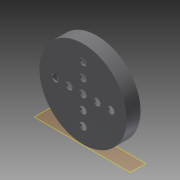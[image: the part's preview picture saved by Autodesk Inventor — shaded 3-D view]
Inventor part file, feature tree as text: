
AUTODESK INVENTOR PART (.ipt)
format: ipt  version: 2015 (Build 190159000, 159)  size: 233,472 bytes
history: native  units: mm
features: extrude x7, sketch x7, projected_geometry x2, plane x1
ambient origin geometry x8: Origin, YZ Plane, XZ Plane, XY Plane, X Axis, Y Axis, Z Axis, Center Point
bodies: Solid1 (feature_tree)
feature tree (17):
  extrude  "Extrusion1"  Depth=20.0mm TaperAngle=0.0deg
  extrude  "Extrusion2"  Depth=2.5mm TaperAngle=0.0deg
  extrude  "Extrusion3"  Depth=15.0mm
  extrude  "Extrusion4"  Depth=10.0mm
  plane  "Work Plane1"
  extrude  "Extrusion5"  Depth=10.0mm
  extrude  "Extrusion6"  Depth=10.0mm
  extrude  "Extrusion7"  Depth=10.0mm
  sketch  "Sketch1"  dims[d0=125.0mm d1=20.0mm d2=0.0mm]
  sketch  "Sketch2"  dims[d3=120.0mm d4=2.5mm d5=0.0mm]
  sketch  "Sketch3"  dims[d6=115.0mm d7=15.0mm]
  sketch  "Sketch4"  dims[d8=0.0mm d9=10.0mm]
  sketch  "Sketch5"  dims[d10=10.0mm d11=10.0mm]
  projected_geometry  "Projected Loop1"
  sketch  "Sketch6"  dims[d12=10.0mm d13=10.0mm]
  sketch  "Sketch7"  dims[d14=10.0mm d15=10.0mm d16=10.0mm d17=10.0mm d18=20.0mm d19=20.0mm d20=20.0mm d21=20.0mm d22=20.0mm d23=20.0mm d24=20.0mm d25=20.0mm d26=17.5mm d27=0.0mm d28=8.5mm d29=4.5mm d30=17.5mm d31=0.0mm d32=50.0mm d33=50.0mm d34=45.0deg d35=50.0mm d36=50.0mm d37=45.0deg d38=50.0mm d39=50.0mm d40=135.0deg d41=50.0mm d42=180.0deg d43=50.0mm d44=135.0deg d45=4.0mm d46=4.0mm d47=4.0mm d48=4.0mm d49=4.0mm d50=4.0mm d51=4.0mm d52=4.0mm d53=17.5mm d54=0.0mm d56=18.0mm d57=43.0mm d58=2.5mm d59=10.0mm d60=0.0mm d61=3.0mm]
  projected_geometry  "Projected Loop2"
